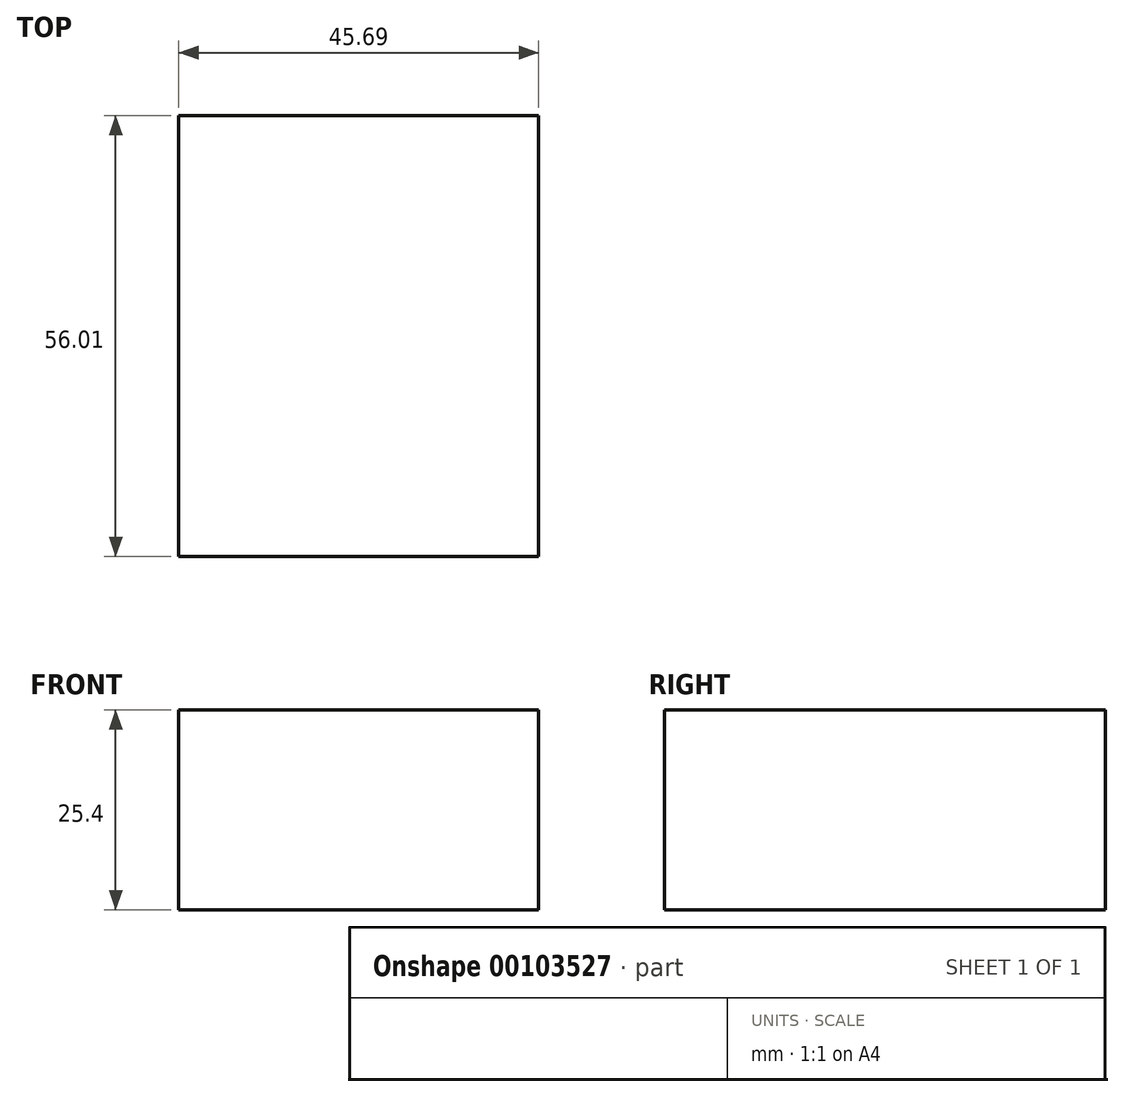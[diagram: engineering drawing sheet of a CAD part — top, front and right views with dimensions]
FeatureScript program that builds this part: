
annotation { "Feature Type Name" : "Feature", "Feature Type Description" : "" }
export const myFeature = defineFeature(function(context is Context, id is Id, definition is map)
    precondition{}
    {
        {
            var Q0;
            Q0=qCreatedBy(makeId("Top.planeOp"),FACE);
            var sketch = newSketch(context, id + "F0", { "sketchPlane" : qUnion([Q0])});
            skLineSegment(sketch, "E0.bottom", {"start": v(-36.4, -24.77) * mm, "end": v(9.3, -24.77) * mm});
            skLineSegment(sketch, "E0.top", {"start": v(-36.4, 31.24) * mm, "end": v(9.3, 31.24) * mm});
            skLineSegment(sketch, "E0.left", {"start": v(-36.4, -24.77) * mm, "end": v(-36.4, 31.24) * mm});
            skLineSegment(sketch, "E0.right", {"start": v(9.3, -24.77) * mm, "end": v(9.3, 31.24) * mm});
            skSolve(sketch);
        }
        {
            var Q0;
            Q0 = qSketchRegion(id + "F0", true);
            extrude(context, id + "F1", {"entities" : qUnion([Q0]), "depth" : 25.4 * mm});
        }
    });
